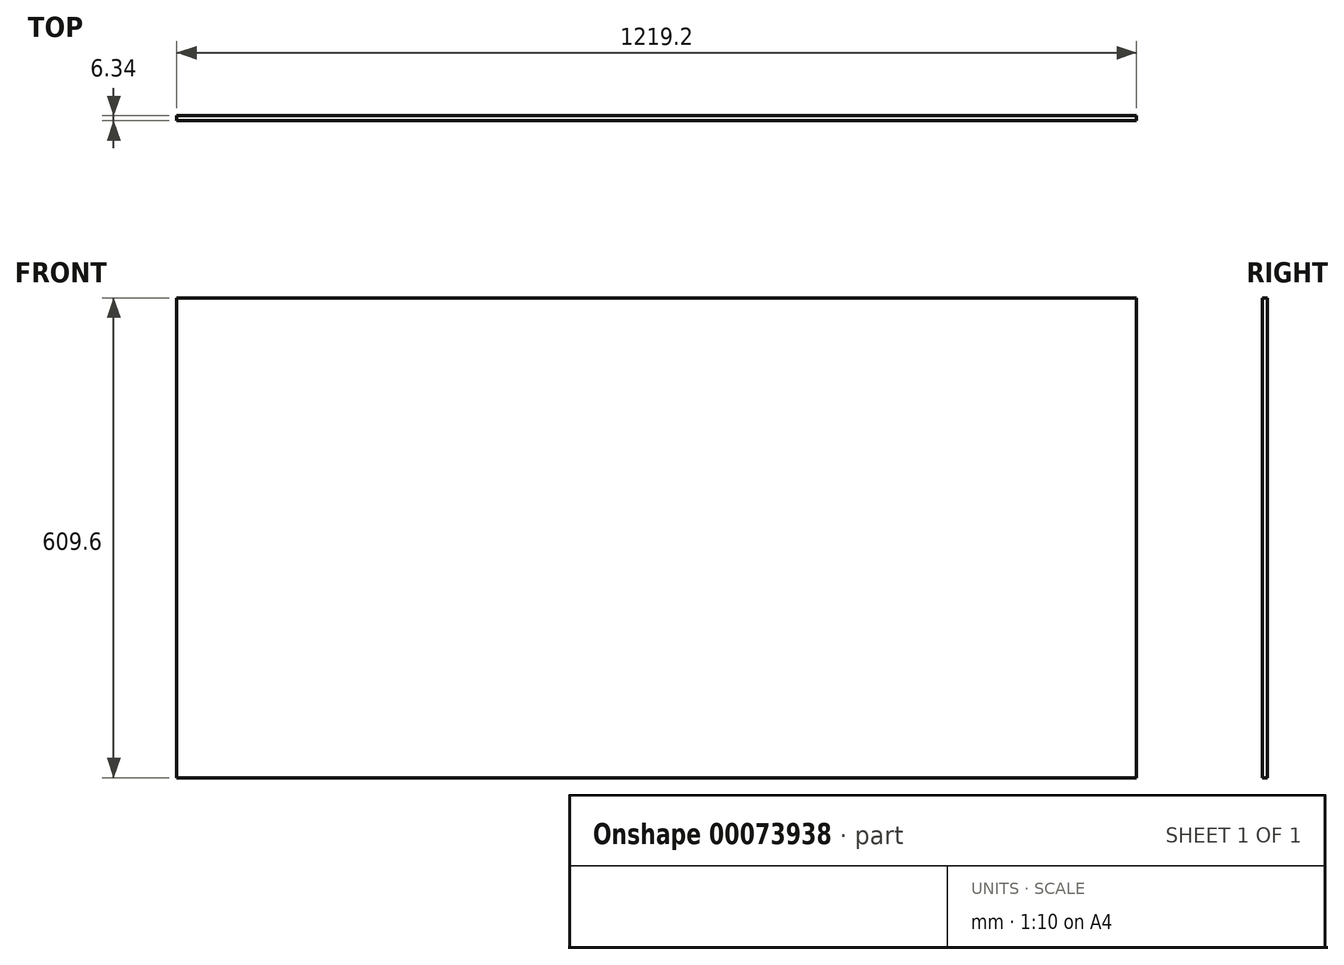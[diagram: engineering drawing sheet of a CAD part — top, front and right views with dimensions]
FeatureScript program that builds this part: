
annotation { "Feature Type Name" : "Feature", "Feature Type Description" : "" }
export const myFeature = defineFeature(function(context is Context, id is Id, definition is map)
    precondition{}
    {
        {
            var Q0;
            Q0=qCreatedBy(makeId("Front.planeOp"),FACE);
            var sketch = newSketch(context, id + "F0", { "sketchPlane" : qUnion([Q0])});
            skLineSegment(sketch, "E0.rect.bottom", {"start": v(-609.6, 304.8) * mm, "end": v(609.6, 304.8) * mm});
            skLineSegment(sketch, "E0.rect.top", {"start": v(-609.6, -304.8) * mm, "end": v(609.6, -304.8) * mm});
            skLineSegment(sketch, "E0.rect.left", {"start": v(-609.6, 304.8) * mm, "end": v(-609.6, -304.8) * mm});
            skLineSegment(sketch, "E0.rect.right", {"start": v(609.6, 304.8) * mm, "end": v(609.6, -304.8) * mm});
            skPoint(sketch, "E0.rect.middle", {"position": v(0, 0) * mm});
            skSolve(sketch);
        }
        {
            var Q0;
            Q0 = qSketchRegion(id + "F0", true);
            extrude(context, id + "F1", {"entities" : qUnion([Q0]), "endBound" : BoundingType.SYMMETRIC, "depth" : 6.35 * mm});
        }
    });
